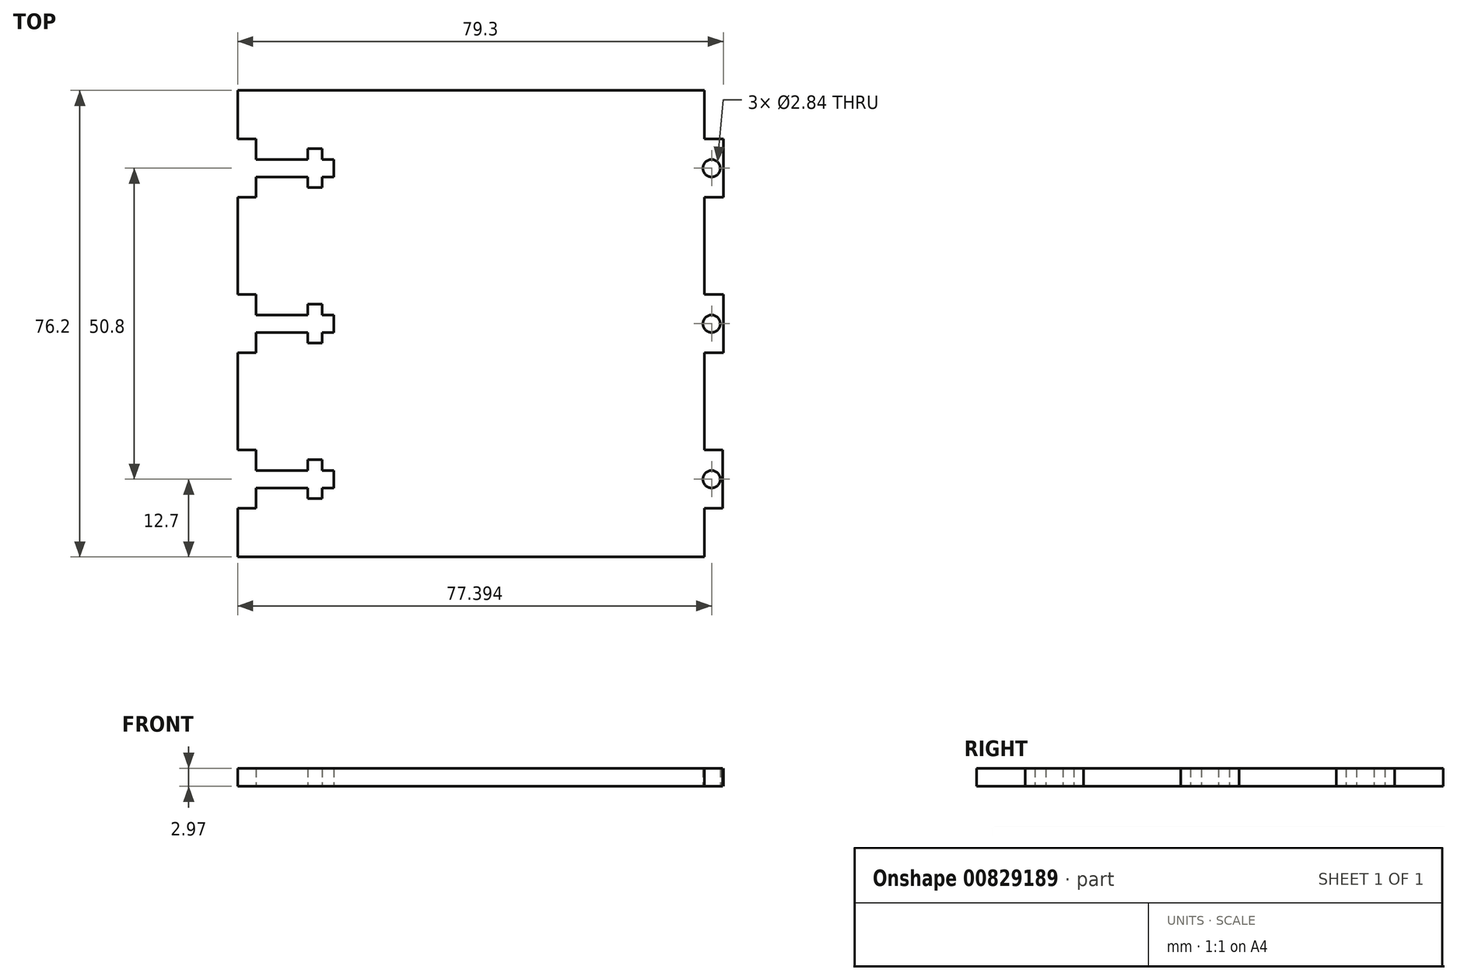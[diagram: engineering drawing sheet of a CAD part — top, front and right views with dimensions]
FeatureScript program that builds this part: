
annotation { "Feature Type Name" : "Feature", "Feature Type Description" : "" }
export const myFeature = defineFeature(function(context is Context, id is Id, definition is map)
    precondition{}
    {
        {
            var Q0;
            Q0=qCreatedBy(makeId("Top.planeOp"),FACE);
            var sketch = newSketch(context, id + "F0", { "sketchPlane" : qUnion([Q0])});
            skLineSegment(sketch, "E0.bottom", {"start": v(0, 0) * mm, "end": v(76.2, 0) * mm});
            skLineSegment(sketch, "E0.top", {"start": v(0, 76.2) * mm, "end": v(76.2, 76.2) * mm});
            skLineSegment(sketch, "E0.left", {"start": v(0, 0) * mm, "end": v(0, 7.94) * mm});
            skLineSegment(sketch, "E0.right", {"start": v(76.2, 0) * mm, "end": v(76.2, 7.94) * mm});
            skLineSegment(sketch, "E1.bottom", {"start": v(0, 68.26) * mm, "end": v(2.97, 68.26) * mm});
            skLineSegment(sketch, "E1.top", {"start": v(0, 58.74) * mm, "end": v(2.97, 58.74) * mm});
            skLineSegment(sketch, "E1.right", {"start": v(2.97, 68.26) * mm, "end": v(2.97, 64.92) * mm});
            skLineSegment(sketch, "E2.0.1.0", {"start": v(0, 42.86) * mm, "end": v(2.97, 42.86) * mm});
            skLineSegment(sketch, "E2.0.1.1", {"start": v(2.97, 42.86) * mm, "end": v(2.97, 39.52) * mm});
            skLineSegment(sketch, "E2.0.1.2", {"start": v(0, 33.34) * mm, "end": v(2.97, 33.34) * mm});
            skLineSegment(sketch, "E2.0.2.0", {"start": v(0, 17.46) * mm, "end": v(2.97, 17.46) * mm});
            skLineSegment(sketch, "E2.0.2.1", {"start": v(2.97, 17.46) * mm, "end": v(2.97, 14.12) * mm});
            skLineSegment(sketch, "E2.0.2.2", {"start": v(0, 7.94) * mm, "end": v(2.97, 7.94) * mm});
            skLineSegment(sketch, "E2.direction2", {"start": v(0, 58.74) * mm, "end": v(0, 42.86) * mm, "construction": true});
            skLineSegment(sketch, "E3.1.0.0", {"start": v(76.2, 42.86) * mm, "end": v(79.3, 42.86) * mm});
            skLineSegment(sketch, "E3.1.0.1", {"start": v(79.3, 42.86) * mm, "end": v(79.3, 33.34) * mm});
            skLineSegment(sketch, "E3.1.0.2", {"start": v(76.2, 33.34) * mm, "end": v(79.3, 33.34) * mm});
            skLineSegment(sketch, "E3.1.0.4", {"start": v(76.2, 17.46) * mm, "end": v(79.17, 17.46) * mm});
            skLineSegment(sketch, "E3.1.0.5", {"start": v(79.17, 17.46) * mm, "end": v(79.17, 7.94) * mm});
            skLineSegment(sketch, "E3.1.0.6", {"start": v(76.2, 7.94) * mm, "end": v(79.17, 7.94) * mm});
            skLineSegment(sketch, "E3.direction1", {"start": v(0, 42.86) * mm, "end": v(76.2, 42.86) * mm, "construction": true});
            skLineSegment(sketch, "E4.0.1.0", {"start": v(76.2, 68.26) * mm, "end": v(79.3, 68.26) * mm});
            skLineSegment(sketch, "E4.0.1.1", {"start": v(79.3, 68.26) * mm, "end": v(79.3, 58.74) * mm});
            skLineSegment(sketch, "E4.0.1.2", {"start": v(76.2, 58.74) * mm, "end": v(79.3, 58.74) * mm});
            skLineSegment(sketch, "E4.direction1", {"start": v(76.2, 42.86) * mm, "end": v(101.6, 42.86) * mm, "construction": true});
            skLineSegment(sketch, "E4.direction2", {"start": v(76.2, 42.86) * mm, "end": v(76.2, 58.74) * mm, "construction": true});
            skLineSegment(sketch, "E5.trimOffspring", {"start": v(0, 68.26) * mm, "end": v(0, 76.2) * mm});
            skLineSegment(sketch, "E6.trimOffspring", {"start": v(0, 42.86) * mm, "end": v(0, 58.74) * mm});
            skLineSegment(sketch, "E7.trimOffspring", {"start": v(0, 17.46) * mm, "end": v(0, 33.34) * mm});
            skLineSegment(sketch, "E8.trimOffspring", {"start": v(76.2, 68.26) * mm, "end": v(76.2, 76.2) * mm});
            skLineSegment(sketch, "E9.trimOffspring", {"start": v(76.2, 42.86) * mm, "end": v(76.2, 58.74) * mm});
            skLineSegment(sketch, "E10.trimOffspring", {"start": v(76.2, 17.46) * mm, "end": v(76.2, 33.34) * mm});
            skLineSegment(sketch, "E11", {"start": v(2.97, 63.5) * mm, "end": v(25.02, 63.5) * mm, "construction": true});
            skLineSegment(sketch, "E12.bottom", {"start": v(2.97, 64.92) * mm, "end": v(11.44, 64.92) * mm});
            skLineSegment(sketch, "E12.top", {"start": v(2.97, 62.08) * mm, "end": v(11.44, 62.08) * mm});
            skLineSegment(sketch, "E12.right", {"start": v(15.67, 64.92) * mm, "end": v(15.67, 62.08) * mm});
            skLineSegment(sketch, "E13.bottom", {"start": v(11.44, 66.68) * mm, "end": v(13.82, 66.68) * mm});
            skLineSegment(sketch, "E13.top", {"start": v(11.44, 60.33) * mm, "end": v(13.82, 60.33) * mm});
            skLineSegment(sketch, "E13.left", {"start": v(11.44, 66.68) * mm, "end": v(11.44, 64.92) * mm});
            skLineSegment(sketch, "E13.right", {"start": v(13.82, 66.68) * mm, "end": v(13.82, 64.92) * mm});
            skLineSegment(sketch, "E14.trimOffspring", {"start": v(11.44, 62.08) * mm, "end": v(11.44, 60.33) * mm});
            skLineSegment(sketch, "E15.trimOffspring", {"start": v(13.82, 64.92) * mm, "end": v(15.67, 64.92) * mm});
            skLineSegment(sketch, "E16.trimOffspring", {"start": v(13.82, 62.08) * mm, "end": v(13.82, 60.33) * mm});
            skLineSegment(sketch, "E17.trimOffspring", {"start": v(13.82, 62.08) * mm, "end": v(15.67, 62.08) * mm});
            skLineSegment(sketch, "E18.trimOffspring", {"start": v(2.97, 62.08) * mm, "end": v(2.97, 58.74) * mm});
            skLineSegment(sketch, "E19.0.1.0", {"start": v(2.97, 39.52) * mm, "end": v(11.44, 39.52) * mm});
            skLineSegment(sketch, "E19.0.1.1", {"start": v(11.44, 41.28) * mm, "end": v(11.44, 39.52) * mm});
            skLineSegment(sketch, "E19.0.1.2", {"start": v(11.44, 41.28) * mm, "end": v(13.82, 41.28) * mm});
            skLineSegment(sketch, "E19.0.1.3", {"start": v(13.82, 41.28) * mm, "end": v(13.82, 39.52) * mm});
            skLineSegment(sketch, "E19.0.1.4", {"start": v(13.82, 39.52) * mm, "end": v(15.67, 39.52) * mm});
            skLineSegment(sketch, "E19.0.1.5", {"start": v(15.67, 39.52) * mm, "end": v(15.67, 36.68) * mm});
            skLineSegment(sketch, "E19.0.1.6", {"start": v(13.82, 36.68) * mm, "end": v(15.67, 36.68) * mm});
            skLineSegment(sketch, "E19.0.1.7", {"start": v(13.82, 36.68) * mm, "end": v(13.82, 34.93) * mm});
            skLineSegment(sketch, "E19.0.1.8", {"start": v(11.44, 34.93) * mm, "end": v(13.82, 34.93) * mm});
            skLineSegment(sketch, "E19.0.1.9", {"start": v(11.44, 36.68) * mm, "end": v(11.44, 34.93) * mm});
            skLineSegment(sketch, "E19.0.1.10", {"start": v(2.97, 36.68) * mm, "end": v(11.44, 36.68) * mm});
            skLineSegment(sketch, "E19.0.2.0", {"start": v(2.97, 14.12) * mm, "end": v(11.44, 14.12) * mm});
            skLineSegment(sketch, "E19.0.2.1", {"start": v(11.44, 15.88) * mm, "end": v(11.44, 14.12) * mm});
            skLineSegment(sketch, "E19.0.2.2", {"start": v(11.44, 15.88) * mm, "end": v(13.82, 15.88) * mm});
            skLineSegment(sketch, "E19.0.2.3", {"start": v(13.82, 15.88) * mm, "end": v(13.82, 14.12) * mm});
            skLineSegment(sketch, "E19.0.2.4", {"start": v(13.82, 14.12) * mm, "end": v(15.67, 14.12) * mm});
            skLineSegment(sketch, "E19.0.2.5", {"start": v(15.67, 14.12) * mm, "end": v(15.67, 11.28) * mm});
            skLineSegment(sketch, "E19.0.2.6", {"start": v(13.82, 11.28) * mm, "end": v(15.67, 11.28) * mm});
            skLineSegment(sketch, "E19.0.2.7", {"start": v(13.82, 11.28) * mm, "end": v(13.82, 9.53) * mm});
            skLineSegment(sketch, "E19.0.2.8", {"start": v(11.44, 9.53) * mm, "end": v(13.82, 9.53) * mm});
            skLineSegment(sketch, "E19.0.2.9", {"start": v(11.44, 11.28) * mm, "end": v(11.44, 9.53) * mm});
            skLineSegment(sketch, "E19.0.2.10", {"start": v(2.97, 11.28) * mm, "end": v(11.44, 11.28) * mm});
            skLineSegment(sketch, "E19.direction1", {"start": v(2.97, 62.08) * mm, "end": v(28.37, 62.08) * mm, "construction": true});
            skLineSegment(sketch, "E19.direction2", {"start": v(2.97, 62.08) * mm, "end": v(2.97, 39.52) * mm, "construction": true});
            skLineSegment(sketch, "E20.trimOffspring", {"start": v(2.97, 36.68) * mm, "end": v(2.97, 33.34) * mm});
            skLineSegment(sketch, "E21.trimOffspring", {"start": v(2.97, 11.28) * mm, "end": v(2.97, 7.94) * mm});
            skCircle(sketch, "E22", {"center": v(77.4, 63.5) * mm, "radius": 1.42 * mm});
            skPoint(sketch, "E22.centerSnap0", {"position": v(79.3, 63.5) * mm});
            skCircle(sketch, "E23.0.1.0", {"center": v(77.4, 38.1) * mm, "radius": 1.42 * mm});
            skLineSegment(sketch, "E23.direction1", {"start": v(77.4, 63.5) * mm, "end": v(102.8, 63.5) * mm, "construction": true});
            skLineSegment(sketch, "E23.direction2", {"start": v(77.4, 63.5) * mm, "end": v(77.4, 38.1) * mm, "construction": true});
            skCircle(sketch, "E24.0.0.2", {"center": v(77.4, 12.7) * mm, "radius": 1.42 * mm});
            skSolve(sketch);
        }
        {
            var Q0;
            Q0=makeQuery(id+"F0.imprint","IMPRINT",FACE,{"disambiguationData":[TD([[makeQuery(id+"F0.imprint","IMPRINT",EDGE,{"derivedFrom":sQuery(id+"F0.wireOp",EDGE,"E0.bottom")}),1.0]])]});
            extrude(context, id + "F1", {"entities" : qUnion([Q0]), "depth" : 2.97 * mm, "offsetDistance" : 25.4 * mm});
        }
    });
